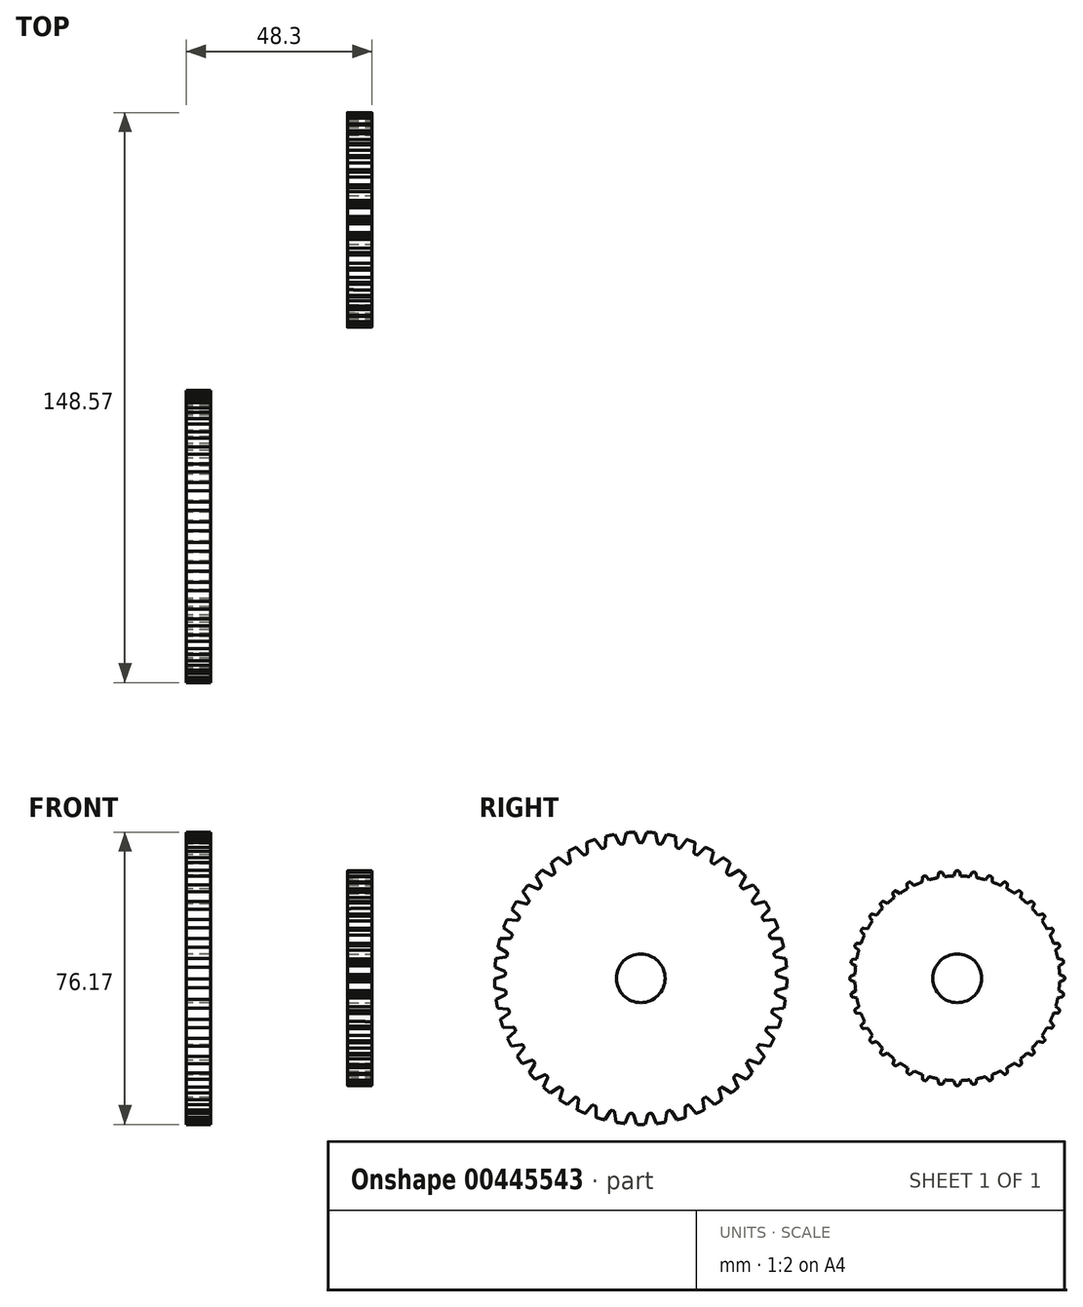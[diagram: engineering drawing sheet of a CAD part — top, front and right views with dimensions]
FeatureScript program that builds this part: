
annotation { "Feature Type Name" : "Feature", "Feature Type Description" : "" }
export const myFeature = defineFeature(function(context is Context, id is Id, definition is map)
    precondition{}
    {
        {
            var Q0;
            Q0=qCreatedBy(makeId("Front.planeOp"),FACE);
            var sketch = newSketch(context, id + "F0", { "sketchPlane" : qUnion([Q0])});
            skLineSegment(sketch, "E0", {"start": v(-6.35, 0) * mm, "end": v(0, 0) * mm, "construction": true});
            skLineSegment(sketch, "E1", {"start": v(0, 38.1) * mm, "end": v(0, -0.58) * mm, "construction": true});
            skLineSegment(sketch, "E2.bottom", {"start": v(0, 38.1) * mm, "end": v(-6.35, 38.1) * mm});
            skLineSegment(sketch, "E2.top", {"start": v(0, 6.35) * mm, "end": v(-6.35, 6.35) * mm});
            skLineSegment(sketch, "E2.left", {"start": v(0, 38.1) * mm, "end": v(0, 6.35) * mm});
            skLineSegment(sketch, "E2.right", {"start": v(-6.35, 38.1) * mm, "end": v(-6.35, 6.35) * mm});
            skSolve(sketch);
        }
        {
            var Q0;
            Q0=makeQuery(id+"F0.imprint","IMPRINT",FACE,{"disambiguationData":[TD([[makeQuery(id+"F0.imprint","IMPRINT",EDGE,{"derivedFrom":sQuery(id+"F0.wireOp",EDGE,"E2.bottom")}),1.0]])]});
            var Q1;
            Q1=sQuery(id+"F0.wireOp",EDGE,"E0");
            revolve(context, id + "F1", {"entities" : qUnion([Q0]), "axis" : qUnion([Q1]), "revolveType" : RevolveType.FULL});
        }
        {
            var Q0;
            Q0=qCreatedBy(makeId("Right.planeOp"),FACE);
            var sketch = newSketch(context, id + "F2", { "sketchPlane" : qUnion([Q0])});
            skLineSegment(sketch, "E3", {"start": v(0, 0) * mm, "end": v(0, 38.15) * mm, "construction": true});
            skArc(sketch, "E4", {"start": v(0.51, 35.34) * mm, "mid": v(0, 35.35) * mm, "end": v(-0.51, 35.34) * mm});
            skLineSegment(sketch, "E5", {"start": v(1.53, 38.13) * mm, "end": v(0.6, 35.6) * mm});
            skLineSegment(sketch, "E6.MirrorCS", {"start": v(-1.53, 38.13) * mm, "end": v(-0.6, 35.6) * mm});
            skLineSegment(sketch, "E7", {"start": v(-0.24, 35.34) * mm, "end": v(0.24, 35.34) * mm});
            skPoint(sketch, "E8.visualSharp", {"position": v(-0.51, 35.34) * mm});
            skArc(sketch, "E8.filletArc", {"start": v(-0.6, 35.6) * mm, "mid": v(-0.46, 35.41) * mm, "end": v(-0.24, 35.34) * mm});
            skPoint(sketch, "E9.visualSharp", {"position": v(0.51, 35.34) * mm});
            skArc(sketch, "E9.filletArc", {"start": v(0.24, 35.34) * mm, "mid": v(0.46, 35.41) * mm, "end": v(0.6, 35.6) * mm});
            skLineSegment(sketch, "E10", {"start": v(-1.53, 38.13) * mm, "end": v(0, 38.15) * mm});
            skLineSegment(sketch, "E11", {"start": v(0, 38.15) * mm, "end": v(1.53, 38.13) * mm});
            skSolve(sketch);
        }
        {
            var Q0;
            Q0=qSketchRegion(id+"F2",true);
            extrude(context, id + "F3", {"entities" : qUnion([Q0]), "operationType" : NewBodyOperationType.REMOVE, "endBound" : BoundingType.SYMMETRIC, "depth" : 12.7 * mm});
        }
        {
            var Q0;
            Q0=makeQuery(id+"F3.boolean.opBoolean","COPY",FACE,{"derivedFrom":makeQuery(id+"F3.opExtrude","SWEPT_FACE",FACE,{"disambiguationData":[OSD([sQuery(id+"F2.wireOp",EDGE,"E6.MirrorCS")])]})});
            var Q1;
            Q1=makeQuery(id+"F3.boolean.opBoolean","COPY",FACE,{"derivedFrom":makeQuery(id+"F3.opExtrude","SWEPT_FACE",FACE,{"disambiguationData":[OSD([sQuery(id+"F2.wireOp",EDGE,"E8.filletArc")])]})});
            var Q2;
            Q2=makeQuery(id+"F3.boolean.opBoolean","COPY",FACE,{"derivedFrom":makeQuery(id+"F3.opExtrude","SWEPT_FACE",FACE,{"disambiguationData":[OSD([sQuery(id+"F2.wireOp",EDGE,"E7")])]})});
            var Q3;
            Q3=makeQuery(id+"F3.boolean.opBoolean","COPY",FACE,{"derivedFrom":makeQuery(id+"F3.opExtrude","SWEPT_FACE",FACE,{"disambiguationData":[OSD([sQuery(id+"F2.wireOp",EDGE,"E9.filletArc")])]})});
            var Q4;
            Q4=makeQuery(id+"F3.boolean.opBoolean","COPY",FACE,{"derivedFrom":makeQuery(id+"F3.opExtrude","SWEPT_FACE",FACE,{"disambiguationData":[OSD([sQuery(id+"F2.wireOp",EDGE,"E5")])]})});
            var Q5;
            Q5=makeQuery(id+"F1.opRevolve","SWEPT_EDGE",EDGE,{"disambiguationData":[OSD([sQuery(id+"F0.wireOp",EDGE,"E2.top"),sQuery(id+"F0.wireOp",EDGE,"E2.left")])]});
            circularPattern(context, id + "F4", {"patternType" : PatternType.FACE, "operationType" : NewBodyOperationType.REMOVE, "faces" : qUnion([Q0, Q1, Q2, Q3, Q4]), "axis" : qUnion([Q5]), "angle" : 8 * degree, "instanceCount" : 45});
        }
        {
            var Q0;
            Q0=qCreatedBy(makeId("Top.planeOp"),FACE);
            var sketch = newSketch(context, id + "F5", { "sketchPlane" : qUnion([Q0])});
            skLineSegment(sketch, "E12", {"start": v(35.6, 109.16) * mm, "end": v(35.6, 88.84) * mm});
            skLineSegment(sketch, "E13", {"start": v(38.77, 88.84) * mm, "end": v(38.77, 109.17) * mm});
            skLineSegment(sketch, "E14.MirrorCS", {"start": v(41.95, 109.18) * mm, "end": v(41.95, 88.84) * mm});
            skLineSegment(sketch, "E15", {"start": v(38.77, 82.5) * mm, "end": v(38.77, 114.37) * mm, "construction": true});
            skLineSegment(sketch, "E16", {"start": v(38.77, 82.5) * mm, "end": v(28.33, 82.5) * mm, "construction": true});
            skLineSegment(sketch, "E17", {"start": v(35.6, 109.16) * mm, "end": v(41.95, 109.18) * mm});
            skLineSegment(sketch, "E18", {"start": v(35.6, 88.84) * mm, "end": v(41.95, 88.84) * mm});
            skSolve(sketch);
        }
        {
            var Q0;
            {var subQ0=sQuery(id+"F5.wireOp",EDGE,"E12");Q0=makeQuery(id+"F5.imprint","IMPRINT",FACE,{"disambiguationData":[TD([[makeQuery(id+"F5.imprint","IMPRINT",EDGE,{"derivedFrom":subQ0}),1.0]])]});}
            var Q1;
            {var subQ0=sQuery(id+"F5.wireOp",EDGE,"E13");Q1=makeQuery(id+"F5.imprint","IMPRINT",FACE,{"disambiguationData":[TD([[makeQuery(id+"F5.imprint","IMPRINT",EDGE,{"derivedFrom":subQ0}),-1.0]])]});}
            var Q2;
            Q2=sQuery(id+"F5.wireOp",EDGE,"E16");
            revolve(context, id + "F6", {"entities" : qUnion([Q0, Q1]), "axis" : qUnion([Q2]), "revolveType" : RevolveType.FULL});
        }
        {
            var Q0;
            Q0=makeQuery(id+"F6.opRevolve","SWEPT_FACE",FACE,{"disambiguationData":[OSD([sQuery(id+"F5.wireOp",EDGE,"E14.MirrorCS")])]});
            var sketch = newSketch(context, id + "F7", { "sketchPlane" : qUnion([Q0])});
            skArc(sketch, "E19", {"start": v(5.08, 22.05) * mm, "mid": v(4.56, 22.05) * mm, "end": v(4.05, 22.05) * mm});
            skLineSegment(sketch, "E20", {"start": v(6.09, 24.83) * mm, "end": v(5.17, 22.3) * mm});
            skArc(sketch, "E21.filletArc", {"start": v(4.8, 22.05) * mm, "mid": v(5.03, 22.12) * mm, "end": v(5.17, 22.3) * mm});
            skLineSegment(sketch, "E22", {"start": v(4.56, 24.85) * mm, "end": v(6.09, 24.83) * mm});
            skLineSegment(sketch, "E23", {"start": v(4.56, 24.85) * mm, "end": v(4.6, 22.05) * mm});
            skArc(sketch, "E24", {"start": v(8.2, 22.26) * mm, "mid": v(7.7, 22.26) * mm, "end": v(7.18, 22.26) * mm});
            skLineSegment(sketch, "E25", {"start": v(9.22, 25.04) * mm, "end": v(8.3, 22.52) * mm});
            skLineSegment(sketch, "E26.MirrorCS", {"start": v(6.16, 25.04) * mm, "end": v(7.08, 22.52) * mm});
            skLineSegment(sketch, "E27", {"start": v(7.45, 22.26) * mm, "end": v(7.93, 22.26) * mm});
            skPoint(sketch, "E28.visualSharp", {"position": v(7.18, 22.26) * mm});
            skArc(sketch, "E28.filletArc", {"start": v(7.08, 22.52) * mm, "mid": v(7.23, 22.33) * mm, "end": v(7.45, 22.26) * mm});
            skPoint(sketch, "E29.visualSharp", {"position": v(8.2, 22.26) * mm});
            skArc(sketch, "E29.filletArc", {"start": v(7.93, 22.26) * mm, "mid": v(8.16, 22.33) * mm, "end": v(8.3, 22.52) * mm});
            skLineSegment(sketch, "E30", {"start": v(6.16, 25.04) * mm, "end": v(7.7, 25.06) * mm});
            skLineSegment(sketch, "E31", {"start": v(7.7, 25.06) * mm, "end": v(9.22, 25.04) * mm});
            skLineSegment(sketch, "E32", {"start": v(7.7, 25.06) * mm, "end": v(7.72, 22.26) * mm});
            skLineSegment(sketch, "E33", {"start": v(82.5, 0) * mm, "end": v(82.5, 39.5) * mm, "construction": true});
            skArc(sketch, "E34", {"start": v(82.02, 27.98) * mm, "mid": v(82.48, 27.97) * mm, "end": v(82.94, 27.97) * mm});
            skLineSegment(sketch, "E35", {"start": v(81.29, 25.92) * mm, "end": v(81.92, 27.72) * mm});
            skLineSegment(sketch, "E36.MirrorCS", {"start": v(83.67, 25.92) * mm, "end": v(83.03, 27.71) * mm});
            skLineSegment(sketch, "E37", {"start": v(82.67, 27.98) * mm, "end": v(82.3, 27.98) * mm});
            skPoint(sketch, "E38.visualSharp", {"position": v(82.94, 27.97) * mm});
            skArc(sketch, "E38.filletArc", {"start": v(83.03, 27.71) * mm, "mid": v(82.9, 27.9) * mm, "end": v(82.67, 27.98) * mm});
            skPoint(sketch, "E39.visualSharp", {"position": v(82.02, 27.98) * mm});
            skArc(sketch, "E39.filletArc", {"start": v(82.3, 27.98) * mm, "mid": v(82.07, 27.9) * mm, "end": v(81.92, 27.72) * mm});
            skLineSegment(sketch, "E40", {"start": v(83.67, 25.92) * mm, "end": v(82.5, 25.92) * mm});
            skLineSegment(sketch, "E41", {"start": v(82.5, 25.92) * mm, "end": v(81.29, 25.92) * mm});
            skLineSegment(sketch, "E42", {"start": v(82.5, 25.92) * mm, "end": v(82.5, 27.97) * mm});
            skSolve(sketch);
        }
        {
            var Q0;
            {var subQ0=sQuery(id+"F7.wireOp",EDGE,"E42");var subQ1=sQuery(id+"F7.wireOp",EDGE,"E34");var subQ2=makeQuery(id+"F7.imprint","INTERSECT",VERTEX,{"derivedFrom":[subQ1,subQ0]});Q0=makeQuery(id+"F7.imprint","IMPRINT",FACE,{"disambiguationData":[TD([[makeQuery(id+"F7.imprint","IMPRINT",EDGE,{"disambiguationData":[TD([[subQ2,1.0]])],"derivedFrom":subQ1}),-1.0]])]});}
            var Q1;
            {var subQ0=sQuery(id+"F7.wireOp",EDGE,"E42");var subQ1=sQuery(id+"F7.wireOp",EDGE,"E34");var subQ2=makeQuery(id+"F7.imprint","INTERSECT",VERTEX,{"derivedFrom":[subQ1,subQ0]});Q1=makeQuery(id+"F7.imprint","IMPRINT",FACE,{"disambiguationData":[TD([[makeQuery(id+"F7.imprint","IMPRINT",EDGE,{"disambiguationData":[TD([[subQ2,-1.0]])],"derivedFrom":subQ1}),-1.0]])]});}
            var Q2;
            {var subQ0=sQuery(id+"F7.wireOp",EDGE,"E41");Q2=makeQuery(id+"F7.imprint","IMPRINT",FACE,{"disambiguationData":[TD([[makeQuery(id+"F7.imprint","IMPRINT",EDGE,{"derivedFrom":subQ0}),-1.0]])]});}
            var Q3;
            {var subQ0=sQuery(id+"F7.wireOp",EDGE,"E40");Q3=makeQuery(id+"F7.imprint","IMPRINT",FACE,{"disambiguationData":[TD([[makeQuery(id+"F7.imprint","IMPRINT",EDGE,{"derivedFrom":subQ0}),-1.0]])]});}
            extrude(context, id + "F8", {"entities" : qUnion([Q0, Q1, Q2, Q3]), "operationType" : NewBodyOperationType.ADD, "oppositeDirection" : true, "depth" : 6.35 * mm});
        }
        {
            var Q0;
            Q0=makeQuery(id+"F8.opExtrude","SWEPT_FACE",FACE,{"disambiguationData":[OSD([sQuery(id+"F7.wireOp",EDGE,"E36.MirrorCS")])]});
            var Q1;
            Q1=makeQuery(id+"F8.opExtrude","SWEPT_FACE",FACE,{"disambiguationData":[OSD([sQuery(id+"F7.wireOp",EDGE,"E38.filletArc")])]});
            var Q2;
            Q2=makeQuery(id+"F8.opExtrude","SWEPT_FACE",FACE,{"disambiguationData":[OSD([sQuery(id+"F7.wireOp",EDGE,"E34")])]});
            var Q3;
            Q3=makeQuery(id+"F8.opExtrude","SWEPT_FACE",FACE,{"disambiguationData":[OSD([sQuery(id+"F7.wireOp",EDGE,"E39.filletArc")])]});
            var Q4;
            Q4=makeQuery(id+"F8.opExtrude","SWEPT_FACE",FACE,{"disambiguationData":[OSD([sQuery(id+"F7.wireOp",EDGE,"E35")])]});
            var Q5;
            Q5=makeQuery(id+"F6.opRevolve","SWEPT_EDGE",EDGE,{"disambiguationData":[OSD([sQuery(id+"F5.wireOp",EDGE,"E14.MirrorCS"),sQuery(id+"F5.wireOp",EDGE,"E18")])]});
            circularPattern(context, id + "F9", {"patternType" : PatternType.FACE, "faces" : qUnion([Q0, Q1, Q2, Q3, Q4]), "axis" : qUnion([Q5]), "angle" : 360 * degree, "instanceCount" : 40, "equalSpace" : true});
        }
    });
